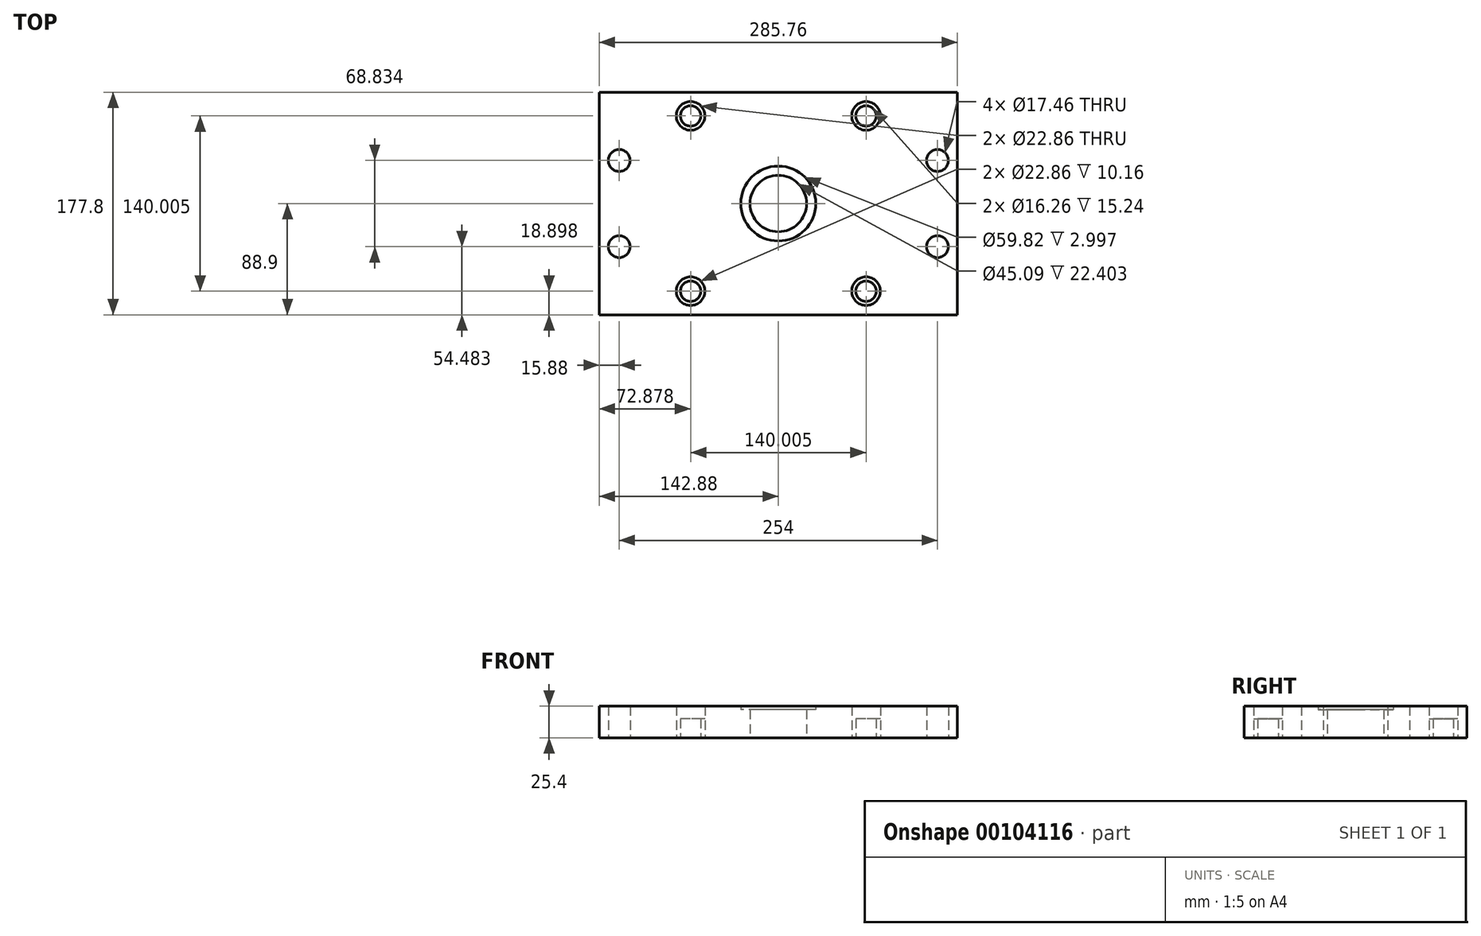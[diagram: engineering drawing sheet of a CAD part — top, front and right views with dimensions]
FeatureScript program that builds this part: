
annotation { "Feature Type Name" : "Feature", "Feature Type Description" : "" }
export const myFeature = defineFeature(function(context is Context, id is Id, definition is map)
    precondition{}
    {
        {
            var Q0;
            Q0=qCreatedBy(makeId("Top.planeOp"),FACE);
            var sketch = newSketch(context, id + "F0", { "sketchPlane" : qUnion([Q0])});
            skCircle(sketch, "E0", {"center": v(0, 0) * mm, "radius": 29.9 * mm});
            skCircle(sketch, "E1", {"center": v(0, 0) * mm, "radius": 22.54 * mm});
            skLineSegment(sketch, "E2.bottom", {"start": v(0, 0) * mm, "end": v(0, 0) * mm});
            skLineSegment(sketch, "E2.top", {"start": v(0, 70) * mm, "end": v(0, 70) * mm});
            skCircle(sketch, "E3", {"center": v(-127, 34.42) * mm, "radius": 8.73 * mm});
            skCircle(sketch, "E4.MirrorC", {"center": v(127, 34.42) * mm, "radius": 8.73 * mm});
            skCircle(sketch, "E5.MirrorC", {"center": v(-127, -34.42) * mm, "radius": 8.73 * mm});
            skCircle(sketch, "E6.MirrorC", {"center": v(127, -34.42) * mm, "radius": 8.73 * mm});
            skCircle(sketch, "E7", {"center": v(70, 70) * mm, "radius": 8.13 * mm});
            skCircle(sketch, "E8.MirrorC", {"center": v(70, -70) * mm, "radius": 8.13 * mm});
            skCircle(sketch, "E9.MirrorC", {"center": v(-70, 70) * mm, "radius": 8.13 * mm});
            skCircle(sketch, "E10.MirrorC", {"center": v(-70, -70) * mm, "radius": 8.13 * mm});
            skLineSegment(sketch, "E11.bottom", {"start": v(-142.88, 88.9) * mm, "end": v(142.88, 88.9) * mm});
            skLineSegment(sketch, "E11.top", {"start": v(-142.88, -88.9) * mm, "end": v(142.88, -88.9) * mm});
            skLineSegment(sketch, "E11.left", {"start": v(-142.88, 88.9) * mm, "end": v(-142.88, -88.9) * mm});
            skLineSegment(sketch, "E11.right", {"start": v(142.88, 88.9) * mm, "end": v(142.88, -88.9) * mm});
            skCircle(sketch, "E12", {"center": v(-70, 70) * mm, "radius": 11.43 * mm});
            skCircle(sketch, "E13.MirrorC", {"center": v(70, 70) * mm, "radius": 11.43 * mm});
            skCircle(sketch, "E14.MirrorC", {"center": v(-70, -70) * mm, "radius": 11.43 * mm});
            skCircle(sketch, "E15.MirrorC", {"center": v(70, -70) * mm, "radius": 11.43 * mm});
            skSolve(sketch);
        }
        {
            var Q0;
            Q0=makeQuery(id+"F0.imprint","IMPRINT",FACE,{"disambiguationData":[TD([[makeQuery(id+"F0.imprint","IMPRINT",EDGE,{"derivedFrom":sQuery(id+"F0.wireOp",EDGE,"E0")}),-1.0]])]});
            extrude(context, id + "F1", {"entities" : qUnion([Q0]), "depth" : 25.4 * mm});
        }
        {
            var Q0;
            Q0=makeQuery(id+"F0.imprint","IMPRINT",FACE,{"disambiguationData":[TD([[makeQuery(id+"F0.imprint","IMPRINT",EDGE,{"derivedFrom":sQuery(id+"F0.wireOp",EDGE,"E0")}),1.0]])]});
            extrude(context, id + "F2", {"entities" : qUnion([Q0]), "operationType" : NewBodyOperationType.ADD, "depth" : 22.4 * mm});
        }
        {
            var Q0;
            Q0=makeQuery(id+"F0.imprint","IMPRINT",FACE,{"disambiguationData":[TD([[makeQuery(id+"F0.imprint","IMPRINT",EDGE,{"derivedFrom":sQuery(id+"F0.wireOp",EDGE,"E9.MirrorC")}),1.0]])]});
            extrude(context, id + "F3", {"entities" : qUnion([Q0]), "operationType" : NewBodyOperationType.ADD, "depth" : 15.24 * mm});
        }
        {
            var Q0;
            Q0=makeQuery(id+"F0.imprint","IMPRINT",FACE,{"disambiguationData":[TD([[makeQuery(id+"F0.imprint","IMPRINT",EDGE,{"derivedFrom":sQuery(id+"F0.wireOp",EDGE,"E7")}),-1.0]])]});
            extrude(context, id + "F4", {"entities" : qUnion([Q0]), "operationType" : NewBodyOperationType.ADD, "depth" : 15.24 * mm});
        }
        {
            var Q0;
            Q0=makeQuery(id+"F0.imprint","IMPRINT",FACE,{"disambiguationData":[TD([[makeQuery(id+"F0.imprint","IMPRINT",EDGE,{"derivedFrom":sQuery(id+"F0.wireOp",EDGE,"E10.MirrorC")}),-1.0]])]});
            extrude(context, id + "F5", {"entities" : qUnion([Q0]), "operationType" : NewBodyOperationType.ADD, "depth" : 15.24 * mm});
        }
        {
            var Q0;
            Q0=makeQuery(id+"F0.imprint","IMPRINT",FACE,{"disambiguationData":[TD([[makeQuery(id+"F0.imprint","IMPRINT",EDGE,{"derivedFrom":sQuery(id+"F0.wireOp",EDGE,"E8.MirrorC")}),1.0]])]});
            extrude(context, id + "F6", {"entities" : qUnion([Q0]), "operationType" : NewBodyOperationType.ADD, "depth" : 15.24 * mm});
        }
    });
